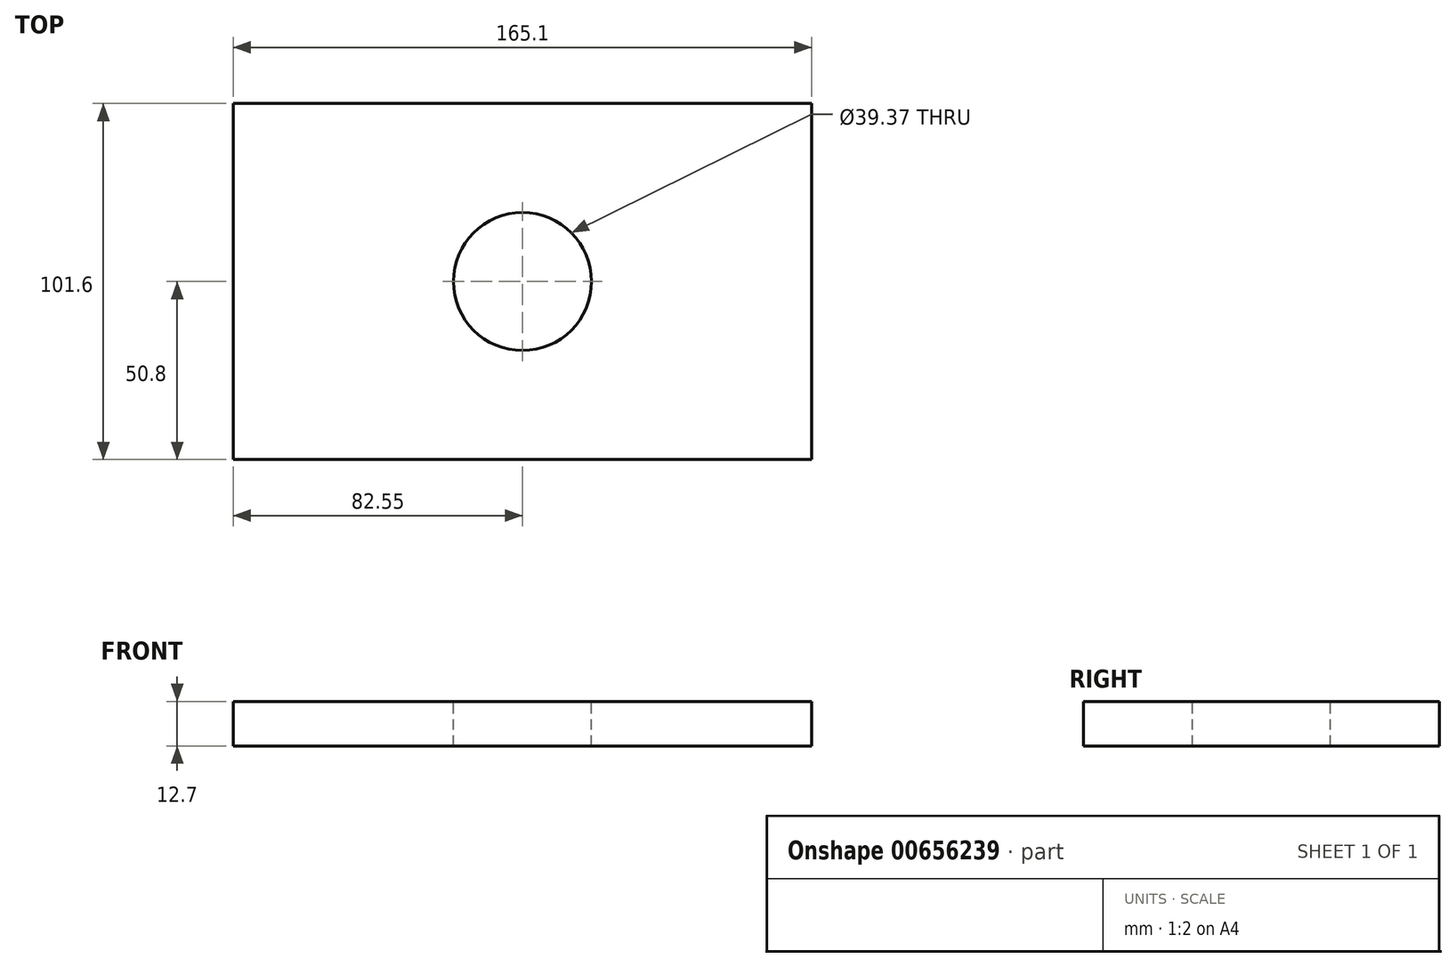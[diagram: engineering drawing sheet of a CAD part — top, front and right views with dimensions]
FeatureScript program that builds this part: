
annotation { "Feature Type Name" : "Feature", "Feature Type Description" : "" }
export const myFeature = defineFeature(function(context is Context, id is Id, definition is map)
    precondition{}
    {
        {
            var Q0;
            Q0=qCreatedBy(makeId("Top.planeOp"),FACE);
            var sketch = newSketch(context, id + "F0", { "sketchPlane" : qUnion([Q0])});
            skLineSegment(sketch, "E0.bottom", {"start": v(-82.55, -50.8) * mm, "end": v(82.55, -50.8) * mm});
            skLineSegment(sketch, "E0.top", {"start": v(-82.55, 50.8) * mm, "end": v(82.55, 50.8) * mm});
            skLineSegment(sketch, "E0.left", {"start": v(-82.55, -50.8) * mm, "end": v(-82.55, 50.8) * mm});
            skLineSegment(sketch, "E0.right", {"start": v(82.55, -50.8) * mm, "end": v(82.55, 50.8) * mm});
            skPoint(sketch, "E0.middle", {"position": v(0, 0) * mm});
            skCircle(sketch, "E1", {"center": v(0, 0) * mm, "radius": 19.69 * mm});
            skSolve(sketch);
        }
        {
            var Q0;
            Q0=makeQuery(id+"F0.imprint","IMPRINT",FACE,{"disambiguationData":[TD([[makeQuery(id+"F0.imprint","IMPRINT",EDGE,{"derivedFrom":sQuery(id+"F0.wireOp",EDGE,"E0.bottom")}),1.0]])]});
            extrude(context, id + "F1", {"entities" : qUnion([Q0]), "oppositeDirection" : true, "depth" : 12.7 * mm, "offsetDistance" : 25.4 * mm});
        }
    });
